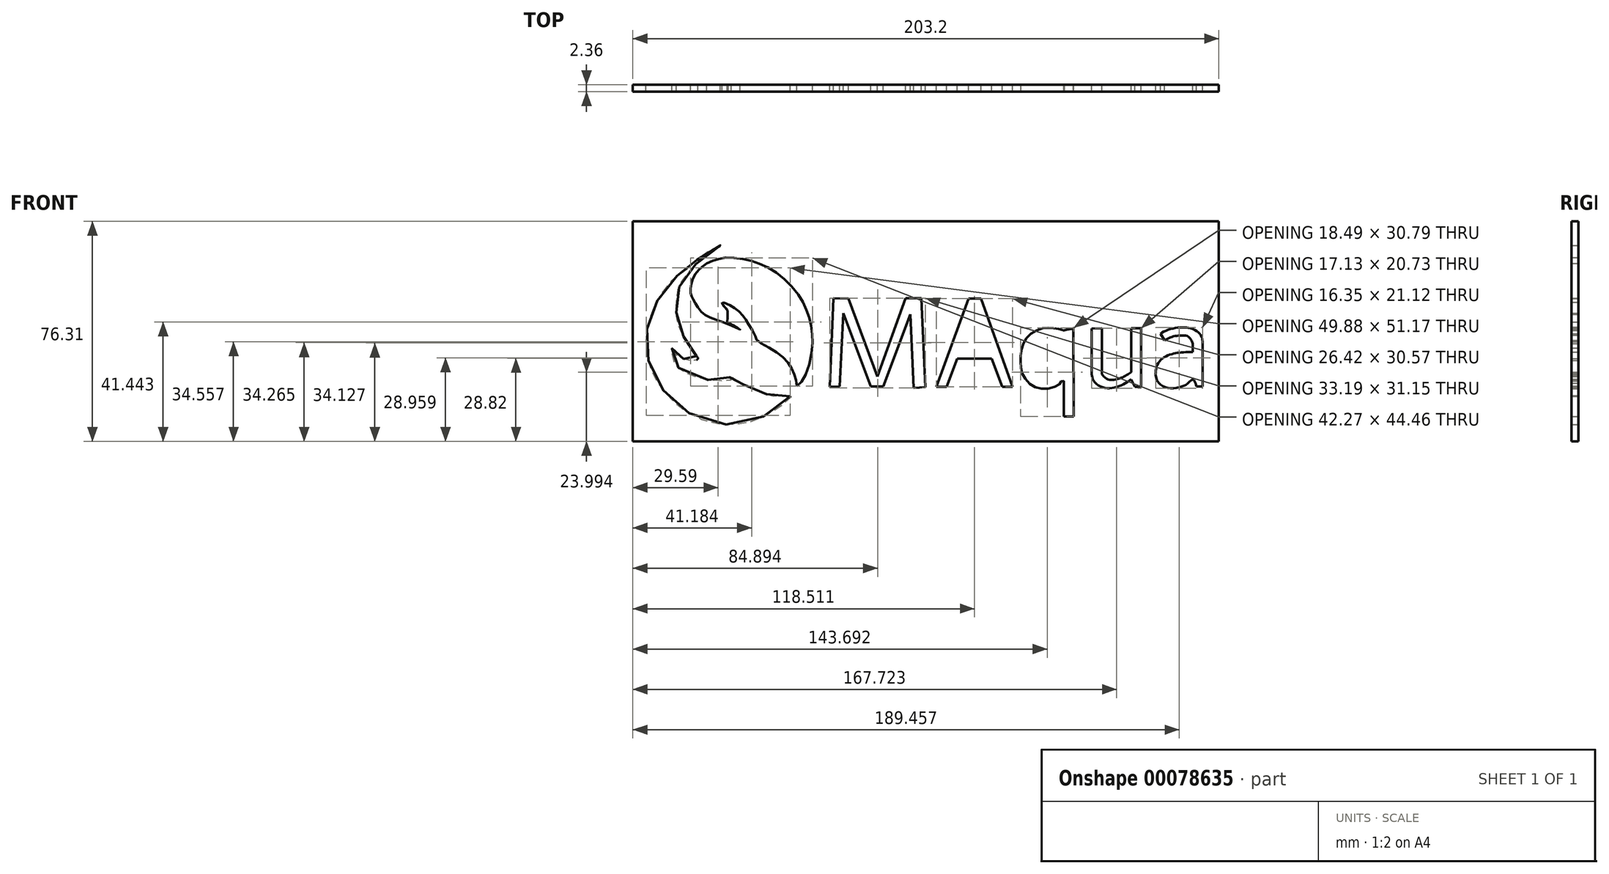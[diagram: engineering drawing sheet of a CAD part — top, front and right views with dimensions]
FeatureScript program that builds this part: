
annotation { "Feature Type Name" : "Feature", "Feature Type Description" : "" }
export const myFeature = defineFeature(function(context is Context, id is Id, definition is map)
    precondition{}
    {
        {
            var Q0;
            Q0=qCreatedBy(makeId("Front.planeOp"),FACE);
            var sketch = newSketch(context, id + "F0", { "sketchPlane" : qUnion([Q0])});
            skPoint(sketch, "E0", {"position": v(-36.29, 6.9) * mm});
            skFitSpline(sketch, "E1", {"points": [v(-44.75, 33.05) * mm, v(-41.53, 34.28) * mm, v(-37.45, 35.03) * mm, v(-30.96, 34.28) * mm, v(-24.95, 32.3) * mm, v(-17.92, 27.74) * mm, v(-12.23, 21.03) * mm, v(-9.66, 15.72) * mm, v(-8.24, 9.85) * mm, v(-8.18, 3) * mm, v(-10.92, -6.71) * mm, v(-13.45, -9.5) * mm], "startDerivative": vector(46.68, 19.35) * mm, "endDerivative": vector(-37.06, -29.38) * mm});
            skFitSpline(sketch, "E2", {"points": [v(-13.45, -9.5) * mm, v(-14.19, -5.77) * mm, v(-16.44, -1.56) * mm, v(-21.12, 2.67) * mm, v(-27.3, 6.36) * mm, v(-27.85, 7.71) * mm, v(-30.28, 12.03) * mm, v(-31.75, 14.3) * mm, v(-34.05, 16.8) * mm, v(-37.02, 18.72) * mm, v(-39.35, 19.42) * mm, v(-38.48, 17.87) * mm, v(-37.37, 16.22) * mm, v(-37.64, 12.64) * mm, v(-37.64, 12.64) * mm], "startDerivative": vector(-6.27, 47.47) * mm, "endDerivative": vector(-18.95, -10.04) * mm});
            skFitSpline(sketch, "E3", {"points": [v(-37.64, 12.64) * mm, v(-33.12, 10.05) * mm, v(-37.64, 12.1) * mm, v(-45.96, 15.62) * mm, v(-49.25, 20.32) * mm, v(-50.26, 22.9) * mm, v(-49.17, 28.55) * mm, v(-44.75, 33.05) * mm], "startDerivative": vector(49.52, -26.74) * mm, "endDerivative": vector(33.65, 25.64) * mm});
            skFitSpline(sketch, "E4", {"points": [v(-15.8, -13.07) * mm, v(-20.77, -13.07) * mm, v(-24.73, -12.06) * mm, v(-29.22, -10.3) * mm, v(-34.85, -7.26) * mm, v(-37.27, -5.77) * mm, v(-36.29, -7.04) * mm, v(-36.29, -7.44) * mm, v(-45.4, -7.22) * mm, v(-53.5, -3.94) * mm, v(-56.1, -0.84) * mm, v(-56.71, 3.1) * mm, v(-56.71, 3.7) * mm, v(-55.88, 2.16) * mm, v(-53.22, 0.1) * mm, v(-48.73, -0.61) * mm, v(-47.74, 0.05) * mm, v(-48.62, 1.27) * mm, v(-50.84, 4.15) * mm, v(-53.83, 10.03) * mm, v(-55.14, 14.4) * mm, v(-55.07, 20.6) * mm, v(-54.06, 25.3) * mm, v(-50.26, 30.68) * mm, v(-44.99, 35.89) * mm, v(-39.98, 39.25) * mm, v(-45.05, 36.54) * mm, v(-51.84, 30.74) * mm, v(-54.94, 28.64) * mm, v(-60.21, 22.84) * mm, v(-64.23, 14.6) * mm, v(-65.61, 8.67) * mm, v(-65.1, -0.15) * mm, v(-61.4, -8.77) * mm, v(-55.42, -15.54) * mm, v(-46, -21.26) * mm, v(-33.34, -22.67) * mm, v(-21.81, -18.27) * mm, v(-15.8, -13.07) * mm]});
            skLineSegment(sketch, "E5", {"start": v(-2.03, -9.8) * mm, "end": v(-0.72, 21) * mm});
            skLineSegment(sketch, "E6", {"start": v(-0.72, 21) * mm, "end": v(4.5, 20.77) * mm});
            skLineSegment(sketch, "E7", {"start": v(4.5, 20.77) * mm, "end": v(14.48, -6.2) * mm});
            skLineSegment(sketch, "E8", {"start": v(14.48, -6.2) * mm, "end": v(24.3, 20.93) * mm});
            skLineSegment(sketch, "E9", {"start": v(24.3, 20.93) * mm, "end": v(29.77, 20.93) * mm});
            skLineSegment(sketch, "E10", {"start": v(29.77, 20.93) * mm, "end": v(31.16, -9.97) * mm});
            skLineSegment(sketch, "E11", {"start": v(31.16, -9.97) * mm, "end": v(27.01, -10.16) * mm});
            skLineSegment(sketch, "E12", {"start": v(27.01, -10.16) * mm, "end": v(25.87, 15.35) * mm});
            skLineSegment(sketch, "E13", {"start": v(25.87, 15.35) * mm, "end": v(16.44, -9.64) * mm});
            skLineSegment(sketch, "E14", {"start": v(16.44, -9.64) * mm, "end": v(12.2, -9.64) * mm});
            skLineSegment(sketch, "E15", {"start": v(12.2, -9.64) * mm, "end": v(2.71, 15.78) * mm});
            skLineSegment(sketch, "E16", {"start": v(2.71, 15.78) * mm, "end": v(1.4, -9.72) * mm});
            skLineSegment(sketch, "E17", {"start": v(1.4, -9.72) * mm, "end": v(-2.03, -9.8) * mm});
            skLineSegment(sketch, "E18", {"start": v(34.97, -9.73) * mm, "end": v(46.15, 20.84) * mm});
            skLineSegment(sketch, "E19", {"start": v(46.15, 20.84) * mm, "end": v(50.39, 20.84) * mm});
            skLineSegment(sketch, "E20", {"start": v(50.39, 20.84) * mm, "end": v(61.39, -9.73) * mm});
            skLineSegment(sketch, "E21", {"start": v(61.39, -9.73) * mm, "end": v(57.84, -9.73) * mm});
            skLineSegment(sketch, "E22", {"start": v(57.84, -9.73) * mm, "end": v(54.11, 0) * mm});
            skLineSegment(sketch, "E23", {"start": v(54.11, 0) * mm, "end": v(42.16, 0) * mm});
            skLineSegment(sketch, "E24", {"start": v(42.16, 0) * mm, "end": v(38.52, -9.73) * mm});
            skLineSegment(sketch, "E25", {"start": v(38.52, -9.73) * mm, "end": v(34.97, -9.73) * mm});
            skLineSegment(sketch, "E26", {"start": v(47.96, 17.03) * mm, "end": v(43.46, 3.52) * mm});
            skLineSegment(sketch, "E27", {"start": v(43.46, 3.52) * mm, "end": v(52.73, 3.52) * mm});
            skLineSegment(sketch, "E28", {"start": v(47.96, 17.03) * mm, "end": v(52.73, 3.52) * mm});
            skFitSpline(sketch, "E29", {"points": [v(79.13, 9.78) * mm, v(82.46, 10.52) * mm], "startDerivative": vector(3.16, 1.1) * mm, "endDerivative": vector(3.16, 1.1) * mm});
            skFitSpline(sketch, "E30", {"points": [v(79.13, 9.78) * mm, v(75.6, 10.52) * mm, v(71.68, 10.52) * mm, v(67.15, 8.15) * mm, v(64.75, 4.16) * mm, v(64.1, -1.13) * mm, v(64.75, -5.22) * mm, v(68.14, -9.37) * mm, v(73.26, -10.46) * mm, v(77.68, -8.77) * mm, v(78.4, -7.73) * mm, v(79.13, -7.8) * mm, v(79.13, -8.5) * mm], "startDerivative": vector(-40.15, 15.12) * mm, "endDerivative": vector(-6.7, -44.02) * mm});
            skLineSegment(sketch, "E31", {"start": v(79.13, -8.5) * mm, "end": v(79.13, -20.11) * mm});
            skLineSegment(sketch, "E32", {"start": v(79.13, -20.11) * mm, "end": v(82.6, -20.11) * mm});
            skLineSegment(sketch, "E33", {"start": v(82.6, -20.11) * mm, "end": v(82.46, 10.52) * mm});
            skLineSegment(sketch, "E34", {"start": v(88.83, 10.45) * mm, "end": v(88.83, -5.52) * mm});
            skFitSpline(sketch, "E35", {"points": [v(88.83, -5.52) * mm, v(89.32, -7.44) * mm, v(92.24, -9.8) * mm, v(96.59, -10.04) * mm, v(100.6, -8.48) * mm, v(102.44, -7.2) * mm], "startDerivative": vector(1.1, -12.1) * mm, "endDerivative": vector(9.72, 7.64) * mm});
            skLineSegment(sketch, "E36", {"start": v(102.44, -7.2) * mm, "end": v(103.75, -9.8) * mm});
            skLineSegment(sketch, "E37", {"start": v(103.75, -9.8) * mm, "end": v(105.96, -9.8) * mm});
            skLineSegment(sketch, "E38", {"start": v(105.96, -9.8) * mm, "end": v(105.96, 10.48) * mm});
            skLineSegment(sketch, "E39", {"start": v(105.96, 10.48) * mm, "end": v(102.54, 10.48) * mm});
            skLineSegment(sketch, "E40", {"start": v(102.54, 10.48) * mm, "end": v(102.54, -4.67) * mm});
            skFitSpline(sketch, "E41", {"points": [v(102.54, -4.67) * mm, v(100.11, -6.17) * mm, v(97.16, -7.27) * mm, v(94.16, -7.1) * mm, v(92.37, -5.48) * mm], "startDerivative": vector(-9.4, -6.26) * mm, "endDerivative": vector(-6.79, 8.35) * mm});
            skLineSegment(sketch, "E42", {"start": v(92.37, -5.48) * mm, "end": v(92.37, 10.48) * mm});
            skLineSegment(sketch, "E43", {"start": v(92.37, 10.48) * mm, "end": v(88.83, 10.45) * mm});
            skFitSpline(sketch, "E44", {"points": [v(114.02, 6.38) * mm, v(116.72, 7.58) * mm, v(119.86, 8.02) * mm, v(121.92, 7.81) * mm, v(123.23, 6.5) * mm, v(123.87, 5.17) * mm], "startDerivative": vector(11.27, 6.07) * mm, "endDerivative": vector(3.33, -8.1) * mm});
            skLineSegment(sketch, "E45", {"start": v(123.87, 5.17) * mm, "end": v(123.87, 2.33) * mm});
            skFitSpline(sketch, "E46", {"points": [v(123.87, 2.33) * mm, v(119.84, 2.15) * mm, v(116.88, 1.64) * mm, v(113.99, 0.47) * mm, v(111.65, -1.91) * mm, v(110.95, -4.9) * mm], "startDerivative": vector(-19, -0.47) * mm, "endDerivative": vector(-1.72, -16.12) * mm});
            skFitSpline(sketch, "E47", {"points": [v(111.12, -4.9) * mm, v(110.95, -4.9) * mm, v(111.46, -7.54) * mm, v(113.85, -9.73) * mm, v(116.9, -10.36) * mm, v(120.1, -9.65) * mm, v(121.95, -8.75) * mm, v(123.73, -7.24) * mm, v(124.22, -7.36) * mm, v(125.1, -9.6) * mm], "startDerivative": vector(-5.78, 2.32) * mm, "endDerivative": vector(6.97, -23) * mm});
            skLineSegment(sketch, "E48", {"start": v(125.1, -9.6) * mm, "end": v(127.3, -9.6) * mm});
            skLineSegment(sketch, "E49", {"start": v(127.3, -9.6) * mm, "end": v(127.3, 5.87) * mm});
            skFitSpline(sketch, "E50", {"points": [v(127.3, 5.87) * mm, v(126.8, 7.82) * mm, v(125.84, 9.01) * mm, v(124.26, 10.1) * mm, v(122.37, 10.64) * mm, v(120.54, 10.83) * mm, v(118.59, 10.76) * mm, v(116.2, 10.25) * mm, v(114, 9.47) * mm, v(112.65, 8.65) * mm], "startDerivative": vector(-3.2, 18.62) * mm, "endDerivative": vector(-12.46, -8.57) * mm});
            skLineSegment(sketch, "E51", {"start": v(112.65, 8.65) * mm, "end": v(114.02, 6.38) * mm});
            skFitSpline(sketch, "E52", {"points": [v(123.74, -4.83) * mm, v(121.66, -6.16) * mm, v(119.03, -7.07) * mm, v(116.57, -7.16) * mm, v(115.3, -6.32) * mm, v(114.72, -4.9) * mm, v(115.2, -3.04) * mm, v(117.12, -1.39) * mm, v(119.42, -0.7) * mm, v(122.57, -0.51) * mm, v(123.67, -0.51) * mm], "startDerivative": vector(-18.41, -13.17) * mm, "endDerivative": vector(11.59, -1.9) * mm});
            skLineSegment(sketch, "E53", {"start": v(123.67, -0.51) * mm, "end": v(123.74, -4.83) * mm});
            skFitSpline(sketch, "E54", {"points": [v(78.92, 7.13) * mm, v(76.48, 7.85) * mm, v(73.73, 7.95) * mm, v(70.88, 6.79) * mm, v(68.78, 4.2) * mm, v(67.86, 0.32) * mm, v(68.06, -2.77) * mm, v(69.54, -5.76) * mm, v(71.67, -7) * mm, v(74.8, -7.17) * mm, v(77.79, -5.62) * mm, v(78.89, -5) * mm], "startDerivative": vector(-28.08, 9.66) * mm, "endDerivative": vector(14.51, 10.98) * mm});
            skLineSegment(sketch, "E55", {"start": v(78.92, 7.13) * mm, "end": v(78.89, -5) * mm});
            skLineSegment(sketch, "E56.bottom", {"start": v(-70.33, 47.6) * mm, "end": v(132.87, 47.6) * mm});
            skLineSegment(sketch, "E56.top", {"start": v(-70.33, -28.71) * mm, "end": v(132.87, -28.71) * mm});
            skLineSegment(sketch, "E56.left", {"start": v(-70.33, 47.6) * mm, "end": v(-70.33, -28.71) * mm});
            skLineSegment(sketch, "E56.right", {"start": v(132.87, 47.6) * mm, "end": v(132.87, -28.71) * mm});
            skSolve(sketch);
        }
        {
            var Q0;
            Q0 = qSketchRegion(id + "F0", true);
            extrude(context, id + "F1", {"entities" : qUnion([Q0]), "depth" : 2.36 * mm});
        }
    });
